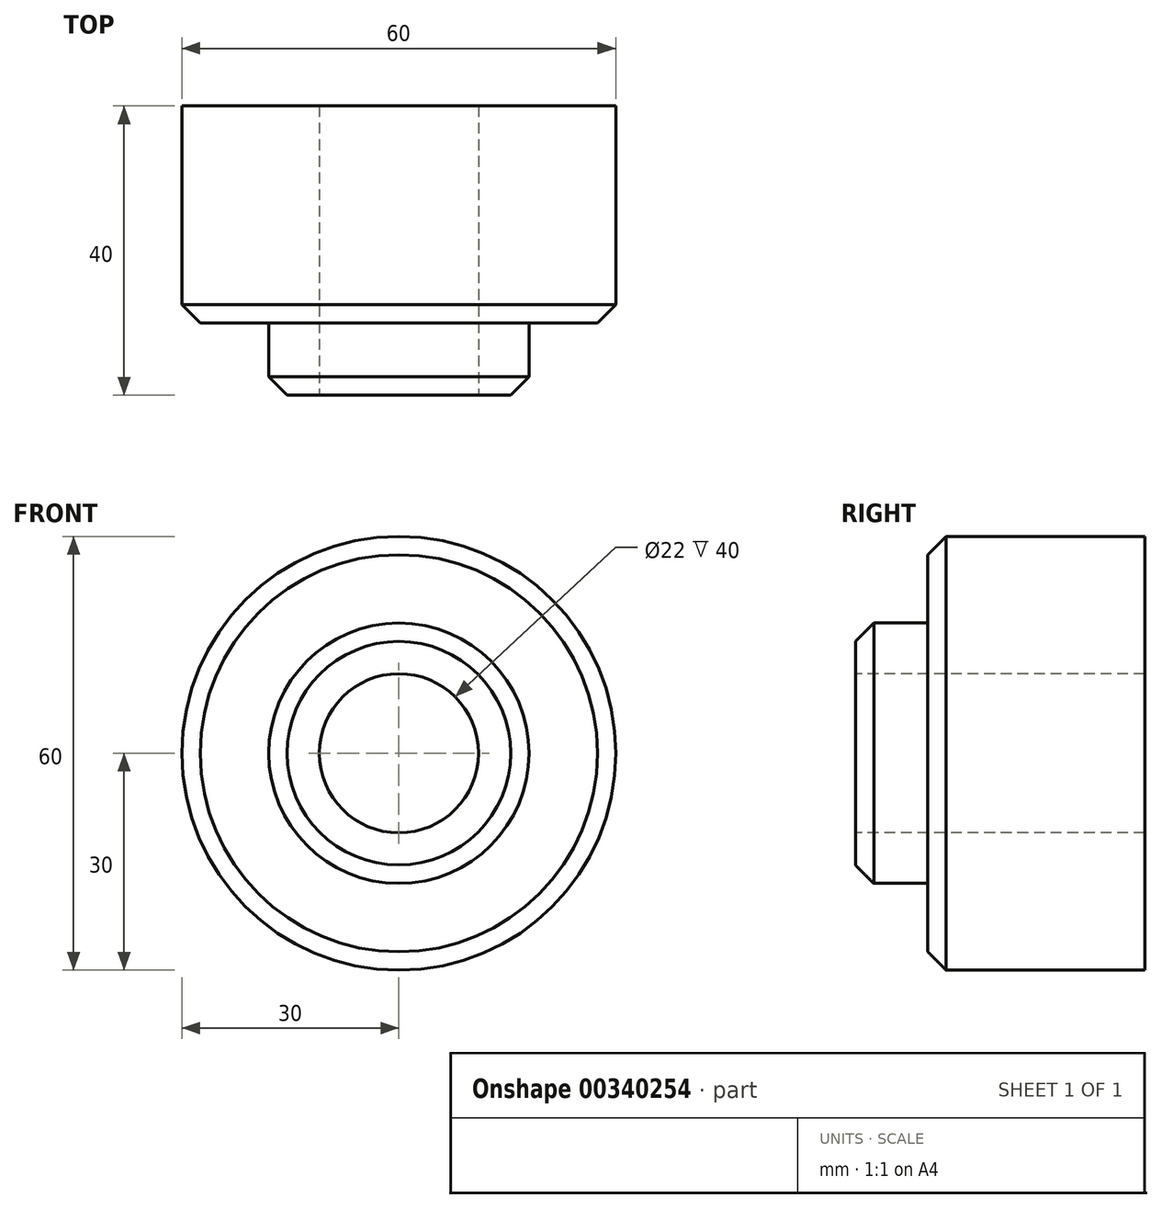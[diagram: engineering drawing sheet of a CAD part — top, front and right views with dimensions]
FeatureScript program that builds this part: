
annotation { "Feature Type Name" : "Feature", "Feature Type Description" : "" }
export const myFeature = defineFeature(function(context is Context, id is Id, definition is map)
    precondition{}
    {
        {
            var Q0;
            Q0=qCreatedBy(makeId("Front.planeOp"),FACE);
            var sketch = newSketch(context, id + "F0", { "sketchPlane" : qUnion([Q0])});
            skCircle(sketch, "E0", {"center": v(0, 0) * mm, "radius": 30 * mm});
            skSolve(sketch);
        }
        {
            var Q0;
            Q0=makeQuery(id+"F0.imprint","IMPRINT",FACE,{"disambiguationData":[TD([[makeQuery(id+"F0.imprint","IMPRINT",EDGE,{"derivedFrom":sQuery(id+"F0.wireOp",EDGE,"E0")}),1.0]])]});
            extrude(context, id + "F1", {"entities" : qUnion([Q0]), "depth" : 30 * mm});
        }
        {
            var Q0;
            Q0=makeQuery(id+"F1.opExtrude","CAP_FACE",FACE,{"disambiguationData":[OSD([sQuery(id+"F0.wireOp",EDGE,"E0")])],"isStart":false});
            var sketch = newSketch(context, id + "F2", { "sketchPlane" : qUnion([Q0])});
            skCircle(sketch, "E1", {"center": v(0, 0) * mm, "radius": 18 * mm});
            skSolve(sketch);
        }
        {
            var Q0;
            Q0=makeQuery(id+"F2.imprint","IMPRINT",FACE,{"disambiguationData":[TD([[makeQuery(id+"F2.imprint","IMPRINT",EDGE,{"derivedFrom":sQuery(id+"F2.wireOp",EDGE,"E1")}),1.0]])]});
            extrude(context, id + "F3", {"entities" : qUnion([Q0]), "operationType" : NewBodyOperationType.ADD, "depth" : 10 * mm});
        }
        {
            var Q0;
            Q0=makeQuery(id+"F3.opExtrude","CAP_FACE",FACE,{"disambiguationData":[OSD([sQuery(id+"F2.wireOp",EDGE,"E1")])],"isStart":false});
            var sketch = newSketch(context, id + "F4", { "sketchPlane" : qUnion([Q0])});
            skCircle(sketch, "E2", {"center": v(0, 0) * mm, "radius": 11 * mm});
            skSolve(sketch);
        }
        {
            var Q0;
            Q0=sQuery(id+"F4.wireOp",VERTEX,"E2.center");
            var Q1;
            Q1=makeQuery(id+"F1.opExtrude","SWEPT_BODY",BODY,{"disambiguationData":[OSD([sQuery(id+"F0.wireOp",EDGE,"E0")])]});
            hole(context, id + "F5", {"style" : HoleStyle.SIMPLE, "endStyle" : HoleEndStyle.THROUGH, "holeDiameter" : 22 * mm, "isTappedThrough" : true, "tappedDepth" : 12.7 * mm, "tapClearance" : 3, "locations" : qUnion([Q0]), "scope" : qUnion([Q1])});
        }
        {
            var Q0;
            Q0=makeQuery(id+"F1.opExtrude","CAP_EDGE",EDGE,{"disambiguationData":[OSD([sQuery(id+"F0.wireOp",EDGE,"E0")])],"isStart":false});
            chamfer(context, id + "F6", {"entities" : qUnion([Q0]), "width" : 2.54 * mm, "tangentPropagation" : true});
        }
        {
            var Q0;
            Q0=makeQuery(id+"F3.opExtrude","CAP_EDGE",EDGE,{"disambiguationData":[OSD([sQuery(id+"F2.wireOp",EDGE,"E1")])],"isStart":false});
            chamfer(context, id + "F7", {"entities" : qUnion([Q0]), "width" : 2.54 * mm, "tangentPropagation" : true});
        }
    });
